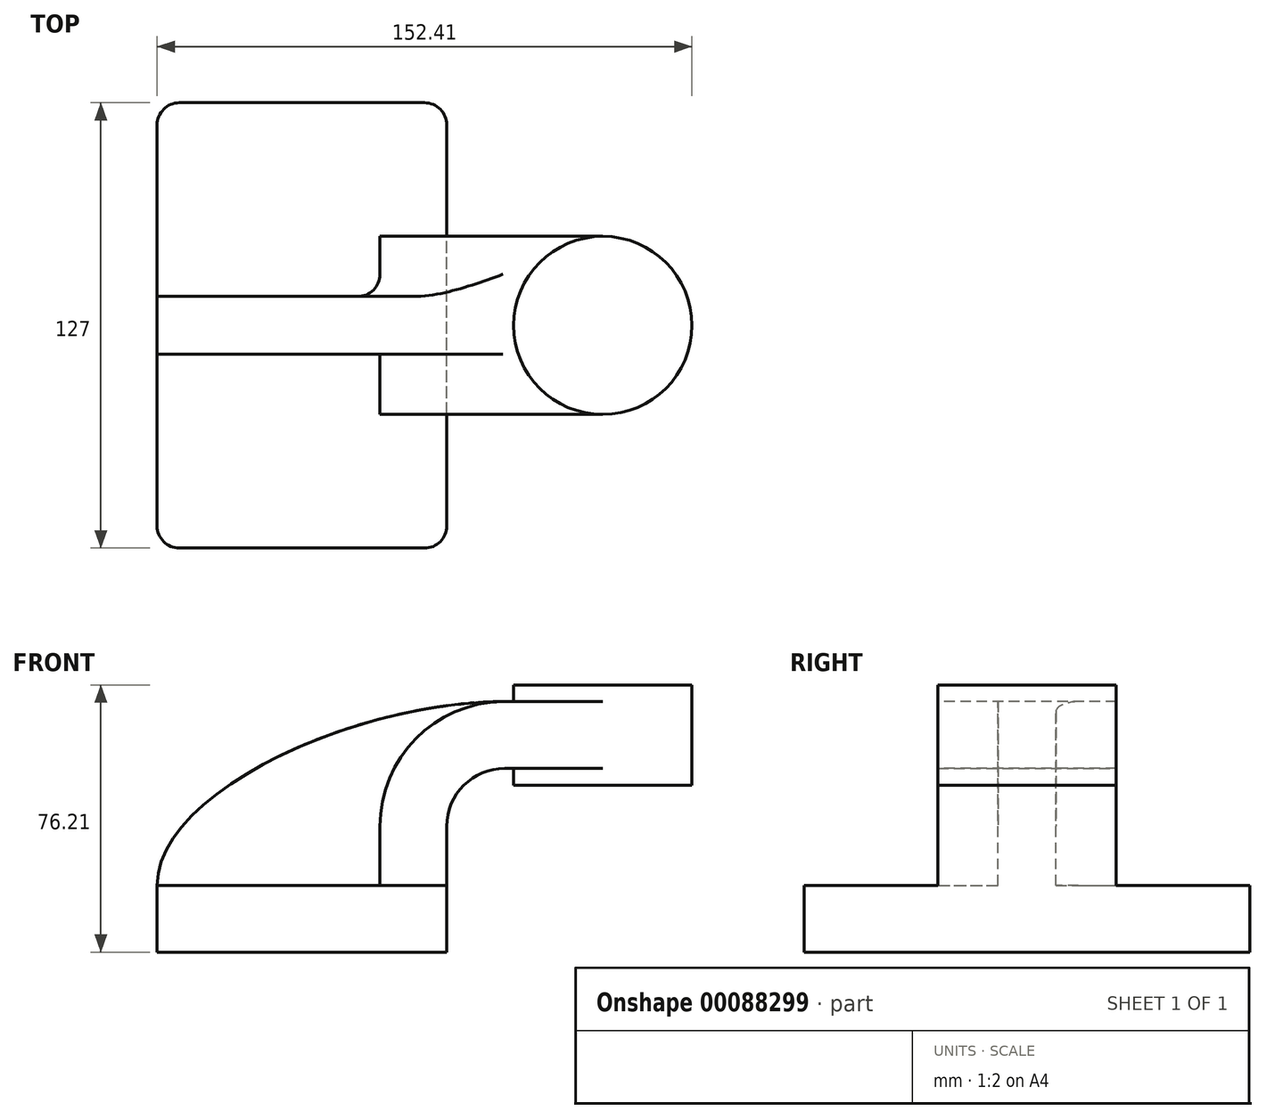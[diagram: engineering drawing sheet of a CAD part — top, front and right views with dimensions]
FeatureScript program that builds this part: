
annotation { "Feature Type Name" : "Feature", "Feature Type Description" : "" }
export const myFeature = defineFeature(function(context is Context, id is Id, definition is map)
    precondition{}
    {
        {
            var Q0;
            Q0=qCreatedBy(makeId("Front.planeOp"),FACE);
            var sketch = newSketch(context, id + "F0", { "sketchPlane" : qUnion([Q0])});
            skLineSegment(sketch, "E0.bottom", {"start": v(41.27, 9.53) * mm, "end": v(-41.28, 9.53) * mm});
            skLineSegment(sketch, "E0.top", {"start": v(41.28, -9.52) * mm, "end": v(-41.27, -9.52) * mm});
            skLineSegment(sketch, "E0.left", {"start": v(41.28, 9.53) * mm, "end": v(41.28, -9.52) * mm});
            skLineSegment(sketch, "E0.right", {"start": v(-41.28, 9.53) * mm, "end": v(-41.27, -9.52) * mm});
            skPoint(sketch, "E0.middle", {"position": v(0, 0) * mm});
            skLineSegment(sketch, "E1.bottom", {"start": v(111.12, 34.93) * mm, "end": v(60.32, 34.93) * mm});
            skLineSegment(sketch, "E1.top", {"start": v(111.12, 66.68) * mm, "end": v(60.32, 66.68) * mm});
            skLineSegment(sketch, "E1.left", {"start": v(111.12, 34.93) * mm, "end": v(111.12, 66.68) * mm});
            skLineSegment(sketch, "E1.right", {"start": v(60.32, 34.93) * mm, "end": v(60.32, 66.68) * mm});
            skPoint(sketch, "E1.middle", {"position": v(85.72, 50.8) * mm});
            skLineSegment(sketch, "E2", {"start": v(41.27, 9.53) * mm, "end": v(41.27, 27) * mm});
            skArc(sketch, "E3", {"start": v(41.27, 27) * mm, "mid": v(45.92, 38.23) * mm, "end": v(57.15, 42.88) * mm});
            skLineSegment(sketch, "E4", {"start": v(57.15, 42.88) * mm, "end": v(85.72, 42.88) * mm});
            skLineSegment(sketch, "E5.0", {"start": v(57.15, 61.93) * mm, "end": v(85.72, 61.93) * mm});
            skArc(sketch, "E5.1", {"start": v(22.23, 27) * mm, "mid": v(32.45, 51.7) * mm, "end": v(57.15, 61.93) * mm});
            skLineSegment(sketch, "E5.2", {"start": v(22.22, 9.53) * mm, "end": v(22.22, 27) * mm});
            skLineSegment(sketch, "E6", {"start": v(85.72, 34.93) * mm, "end": v(85.72, 66.68) * mm});
            skFitSpline(sketch, "E7", {"points": [v(-41.28, 9.53) * mm, v(57.15, 61.93) * mm], "startDerivative": vector(0.9, 64.56) * mm, "endDerivative": vector(121.7, 2.8) * mm});
            skSolve(sketch);
        }
        {
            var Q0;
            Q0=makeQuery(id+"F0.imprint","IMPRINT",FACE,{"disambiguationData":[TD([[makeQuery(id+"F0.imprint","IMPRINT",EDGE,{"derivedFrom":sQuery(id+"F0.wireOp",EDGE,"E0.top")}),-1.0]])]});
            extrude(context, id + "F1", {"entities" : qUnion([Q0]), "endBound" : BoundingType.SYMMETRIC, "depth" : 127 * mm});
        }
        {
            var Q0;
            {var subQ1=sQuery(id+"F0.wireOp",EDGE,"E2");Q0=makeQuery(id+"F0.imprint","IMPRINT",FACE,{"disambiguationData":[TD([[makeQuery(id+"F0.imprint","IMPRINT",EDGE,{"derivedFrom":subQ1}),1.0]])]});}
            var Q1;
            {var subQ0=sQuery(id+"F0.wireOp",EDGE,"E4");var subQ1=sQuery(id+"F0.wireOp",EDGE,"E1.right");var subQ2=makeQuery(id+"F0.imprint","INTERSECT",VERTEX,{"derivedFrom":[subQ1,subQ0]});Q1=makeQuery(id+"F0.imprint","IMPRINT",FACE,{"disambiguationData":[TD([[makeQuery(id+"F0.imprint","IMPRINT",EDGE,{"disambiguationData":[TD([[subQ2,-1.0]])],"derivedFrom":subQ1}),-1.0]])]});}
            extrude(context, id + "F2", {"entities" : qUnion([Q0, Q1]), "operationType" : NewBodyOperationType.ADD, "endBound" : BoundingType.SYMMETRIC, "depth" : 50.8 * mm});
        }
        {
            var Q0;
            {var subQ3=sQuery(id+"F0.wireOp",EDGE,"E5.2");Q0=makeQuery(id+"F0.imprint","IMPRINT",FACE,{"disambiguationData":[TD([[makeQuery(id+"F0.imprint","IMPRINT",EDGE,{"derivedFrom":subQ3}),1.0]])]});}
            extrude(context, id + "F3", {"entities" : qUnion([Q0]), "operationType" : NewBodyOperationType.ADD, "endBound" : BoundingType.SYMMETRIC, "depth" : 15.88 * mm});
        }
        {
            var Q0;
            {var subQ0=sQuery(id+"F0.wireOp",EDGE,"E1.left");Q0=makeQuery(id+"F0.imprint","IMPRINT",FACE,{"disambiguationData":[TD([[makeQuery(id+"F0.imprint","IMPRINT",EDGE,{"derivedFrom":subQ0}),1.0]])]});}
            var Q1;
            Q1=sQuery(id+"F0.wireOp",EDGE,"E6");
            revolve(context, id + "F4", {"operationType" : NewBodyOperationType.ADD, "entities" : qUnion([Q0]), "axis" : qUnion([Q1]), "revolveType" : RevolveType.FULL});
        }
        {
            var Q0;
            Q0=makeQuery(id+"F1.opExtrude","CAP_EDGE",EDGE,{"disambiguationData":[OSD([sQuery(id+"F0.wireOp",EDGE,"E0.right")])],"isStart":false});
            var Q1;
            Q1=makeQuery(id+"F1.opExtrude","CAP_EDGE",EDGE,{"disambiguationData":[OSD([sQuery(id+"F0.wireOp",EDGE,"E0.right")])],"isStart":true});
            var Q2;
            Q2=makeQuery(id+"F1.opExtrude","CAP_EDGE",EDGE,{"disambiguationData":[OSD([sQuery(id+"F0.wireOp",EDGE,"E0.left")])],"isStart":false});
            var Q3;
            Q3=makeQuery(id+"F1.opExtrude","CAP_EDGE",EDGE,{"disambiguationData":[OSD([sQuery(id+"F0.wireOp",EDGE,"E0.left")])],"isStart":true});
            fillet(context, id + "F5", {"entities" : qUnion([Q0, Q1, Q2, Q3]), "radius" : 6.35 * mm, "tangentPropagation" : true, "allowEdgeOverflow" : false});
        }
        {
            var Q0;
            Q0=makeQuery(id+"F1.opExtrude","SWEPT_BODY",BODY,{"disambiguationData":[OSD([sQuery(id+"F0.wireOp",EDGE,"E0.bottom"),sQuery(id+"F0.wireOp",EDGE,"E0.top"),sQuery(id+"F0.wireOp",EDGE,"E0.left"),sQuery(id+"F0.wireOp",EDGE,"E0.right")])]});
            deleteBodies(context, id + "F6", {"entities" : qUnion([Q0])});
        }
        {
            var Q0;
            Q0=qCreatedBy(makeId("Front.planeOp"),FACE);
            var sketch = newSketch(context, id + "F7", { "sketchPlane" : qUnion([Q0])});
            skLineSegment(sketch, "E8.bottom", {"start": v(41.27, 9.53) * mm, "end": v(-41.28, 9.53) * mm});
            skLineSegment(sketch, "E8.top", {"start": v(41.28, -9.52) * mm, "end": v(-41.27, -9.52) * mm});
            skLineSegment(sketch, "E8.left", {"start": v(41.28, 9.53) * mm, "end": v(41.28, -9.52) * mm});
            skLineSegment(sketch, "E8.right", {"start": v(-41.28, 9.53) * mm, "end": v(-41.27, -9.52) * mm});
            skPoint(sketch, "E8.middle", {"position": v(0, 0) * mm});
            skLineSegment(sketch, "E9.bottom", {"start": v(60.33, 38.1) * mm, "end": v(111.13, 38.1) * mm});
            skLineSegment(sketch, "E9.top", {"start": v(60.33, 66.68) * mm, "end": v(111.13, 66.68) * mm});
            skLineSegment(sketch, "E9.left", {"start": v(60.33, 38.1) * mm, "end": v(60.33, 66.68) * mm});
            skLineSegment(sketch, "E9.right", {"start": v(111.13, 38.1) * mm, "end": v(111.13, 66.68) * mm});
            skPoint(sketch, "E9.middle", {"position": v(85.73, 52.39) * mm});
            skLineSegment(sketch, "E10", {"start": v(41.27, 9.53) * mm, "end": v(41.27, 26.37) * mm});
            skArc(sketch, "E11", {"start": v(41.27, 26.37) * mm, "mid": v(46.11, 38.04) * mm, "end": v(57.79, 42.88) * mm});
            skLineSegment(sketch, "E12", {"start": v(57.79, 42.88) * mm, "end": v(85.73, 42.88) * mm});
            skLineSegment(sketch, "E13.0", {"start": v(57.78, 61.93) * mm, "end": v(85.73, 61.93) * mm});
            skArc(sketch, "E13.1", {"start": v(22.22, 26.37) * mm, "mid": v(32.64, 51.5) * mm, "end": v(57.78, 61.93) * mm});
            skLineSegment(sketch, "E13.2", {"start": v(22.22, 9.53) * mm, "end": v(22.22, 26.37) * mm});
            skLineSegment(sketch, "E14", {"start": v(85.73, 66.68) * mm, "end": v(85.73, 38.1) * mm});
            skFitSpline(sketch, "E15", {"points": [v(-41.28, 9.53) * mm, v(57.78, 61.93) * mm], "startDerivative": vector(-0.42, 77.92) * mm, "endDerivative": vector(133.08, 0.69) * mm});
            skSolve(sketch);
        }
        {
            var Q0;
            Q0=makeQuery(id+"F7.imprint","IMPRINT",FACE,{"disambiguationData":[TD([[makeQuery(id+"F7.imprint","IMPRINT",EDGE,{"derivedFrom":sQuery(id+"F7.wireOp",EDGE,"E8.top")}),-1.0]])]});
            extrude(context, id + "F8", {"entities" : qUnion([Q0]), "endBound" : BoundingType.SYMMETRIC, "depth" : 127 * mm});
        }
        {
            var Q0;
            {var subQ0=sQuery(id+"F7.wireOp",EDGE,"E10");Q0=makeQuery(id+"F7.imprint","IMPRINT",FACE,{"disambiguationData":[TD([[makeQuery(id+"F7.imprint","IMPRINT",EDGE,{"derivedFrom":subQ0}),1.0]])]});}
            var Q1;
            {var subQ0=sQuery(id+"F7.wireOp",EDGE,"E12");var subQ1=sQuery(id+"F7.wireOp",EDGE,"E9.left");var subQ2=makeQuery(id+"F7.imprint","INTERSECT",VERTEX,{"derivedFrom":[subQ1,subQ0]});Q1=makeQuery(id+"F7.imprint","IMPRINT",FACE,{"disambiguationData":[TD([[makeQuery(id+"F7.imprint","IMPRINT",EDGE,{"disambiguationData":[TD([[subQ2,-1.0]])],"derivedFrom":subQ1}),-1.0]])]});}
            extrude(context, id + "F9", {"entities" : qUnion([Q0, Q1]), "operationType" : NewBodyOperationType.ADD, "endBound" : BoundingType.SYMMETRIC, "depth" : 50.8 * mm});
        }
        {
            var Q0;
            {var subQ3=sQuery(id+"F7.wireOp",EDGE,"E13.2");Q0=makeQuery(id+"F7.imprint","IMPRINT",FACE,{"disambiguationData":[TD([[makeQuery(id+"F7.imprint","IMPRINT",EDGE,{"derivedFrom":subQ3}),1.0]])]});}
            extrude(context, id + "F10", {"entities" : qUnion([Q0]), "operationType" : NewBodyOperationType.ADD, "endBound" : BoundingType.SYMMETRIC, "depth" : 16.5 * mm});
        }
        {
            var Q0;
            {var subQ0=sQuery(id+"F7.wireOp",EDGE,"E9.right");Q0=makeQuery(id+"F7.imprint","IMPRINT",FACE,{"disambiguationData":[TD([[makeQuery(id+"F7.imprint","IMPRINT",EDGE,{"derivedFrom":subQ0}),1.0]])]});}
            var Q1;
            Q1=sQuery(id+"F7.wireOp",EDGE,"E14");
            revolve(context, id + "F11", {"operationType" : NewBodyOperationType.ADD, "entities" : qUnion([Q0]), "axis" : qUnion([Q1]), "revolveType" : RevolveType.FULL});
        }
        {
            var Q0;
            Q0=makeQuery(id+"F8.opExtrude","CAP_EDGE",EDGE,{"disambiguationData":[OSD([sQuery(id+"F7.wireOp",EDGE,"E8.right")])],"isStart":false});
            var Q1;
            Q1=makeQuery(id+"F8.opExtrude","CAP_EDGE",EDGE,{"disambiguationData":[OSD([sQuery(id+"F7.wireOp",EDGE,"E8.left")])],"isStart":false});
            var Q2;
            Q2=makeQuery(id+"F8.opExtrude","CAP_EDGE",EDGE,{"disambiguationData":[OSD([sQuery(id+"F7.wireOp",EDGE,"E8.left")])],"isStart":true});
            var Q3;
            Q3=makeQuery(id+"F8.opExtrude","CAP_EDGE",EDGE,{"disambiguationData":[OSD([sQuery(id+"F7.wireOp",EDGE,"E8.right")])],"isStart":true});
            var Q4;
            Q4=makeQuery(id+"F10.opExtrude","CAP_EDGE",EDGE,{"disambiguationData":[OSD([sQuery(id+"F7.wireOp",EDGE,"E13.2")])],"isStart":true});
            var Q5;
            Q5=makeQuery(id+"F10.opExtrude","CAP_EDGE",EDGE,{"disambiguationData":[OSD([sQuery(id+"F7.wireOp",EDGE,"E13.2")])],"isStart":false});
            fillet(context, id + "F12", {"entities" : qUnion([Q0, Q1, Q2, Q3, Q4, Q5]), "radius" : 6.35 * mm, "tangentPropagation" : true, "allowEdgeOverflow" : false});
        }
    });
